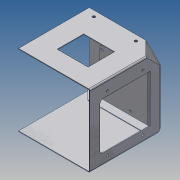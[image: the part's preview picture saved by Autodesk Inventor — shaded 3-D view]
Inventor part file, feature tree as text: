
AUTODESK INVENTOR PART (.ipt)
format: ipt  version: 2017 (Build 210142000, 142)  size: 428,544 bytes
history: native  units: mm
features: other x11, sketch x5, extrude x4, sheet_metal_op x4, hole x2, plane x1
ambient origin geometry x8: Origin, YZ Plane, XZ Plane, XY Plane, X Axis, Y Axis, Z Axis, Center Point
bodies: Solid1 (feature_tree)
feature tree (27):
  plane  "Work Plane1"
  extrude  "Extrusion1"  Depth=1.0mm TaperAngle=0.0deg
  sketch  "Sketch2"  dims[d0=50.0mm d2=1.0mm d3=0.0mm]
  sheet_metal_op  "Face1"
  other  "Pliegue1"
  sheet_metal_op  "Face2"
  other  "Pestaña1"
  sketch  "Boceto5"  dims[d8=2.0mm d9=1.0mm]
  other  "Cara3"
  extrude  "Extrusion2"  Depth=1.0mm
  extrude  "Extrusion3"  Depth=1.0mm
  extrude  "Extrusion4"  Depth=1.0mm
  hole  "Hole2"  [1 undecoded]
  other  "Plate1"
  sheet_metal_op  "Bend1"
  sketch  "Sketch3"  dims[d4=100.0mm d5=1.0mm]
  other  "Plate2"
  sheet_metal_op  "Bend2"
  sketch  "Boceto4"  dims[d6=1.0mm d7=0.5mm]
  other  "Placa3"
  other  "Doblez3"
  other  "Esquina1"
  other  "Placa4"
  other  "Doblez4"
  sketch  "Sketch6"  dims[d10=19.9mm d12=99.8mm d13=20.0mm d14=20.0mm d15=20.0mm d16=20.0mm d17=1.0mm d18=1.0mm d19=0.5mm d20=2.0mm d21=1.0mm d22=100.0mm d23=49.9mm d24=1.0mm d25=0.5mm d26=2.0mm d27=1.0mm d28=15.0mm d29=90.0deg d30=1.0mm d31=4.0mm d32=1.0mm d33=1.0mm d34=1.0mm d35=70.0mm d36=4.0mm d37=65.0mm d38=35.0mm d39=1.0mm d40=0.5mm d41=2.0mm d42=1.0mm d43=90.0deg d44=1.0mm d45=100.0mm d46=50.0mm d47=100.0mm d48=3.5mm d49=3.5mm d50=1.0mm d51=1.0mm d52=0.5mm d53=2.0mm d54=1.0mm d55=3.5mm d56=3.5mm d57=50.0mm d58=100.0mm d59=3.5mm d60=3.5mm d61=50.0mm d62=14.0mm d63=14.0mm d64=3.0mm d65=12.0mm d66=50.0mm d67=4.0mm d68=6.0mm d69=76.014719mm d70=6.0mm d71=6.0mm d72=10.0mm d73=0.0mm d74=10.0mm d75=0.0mm d76=10.0mm d77=0.0mm d78=12.0mm d79=45.0deg d80=12.0mm d81=3.4544mm d82=6.0mm d83=4.0mm d84=2.0mm d85=90.0deg d86=8.0mm d87=0.0mm]
  hole  "Hole1"  [1 undecoded]
  other  "Definición1"
note: 2 required parameter values undecoded (feature->parameter linkage not recoverable at this tier; creation-order binding heuristic only, values carry confidence <= 0.55)
